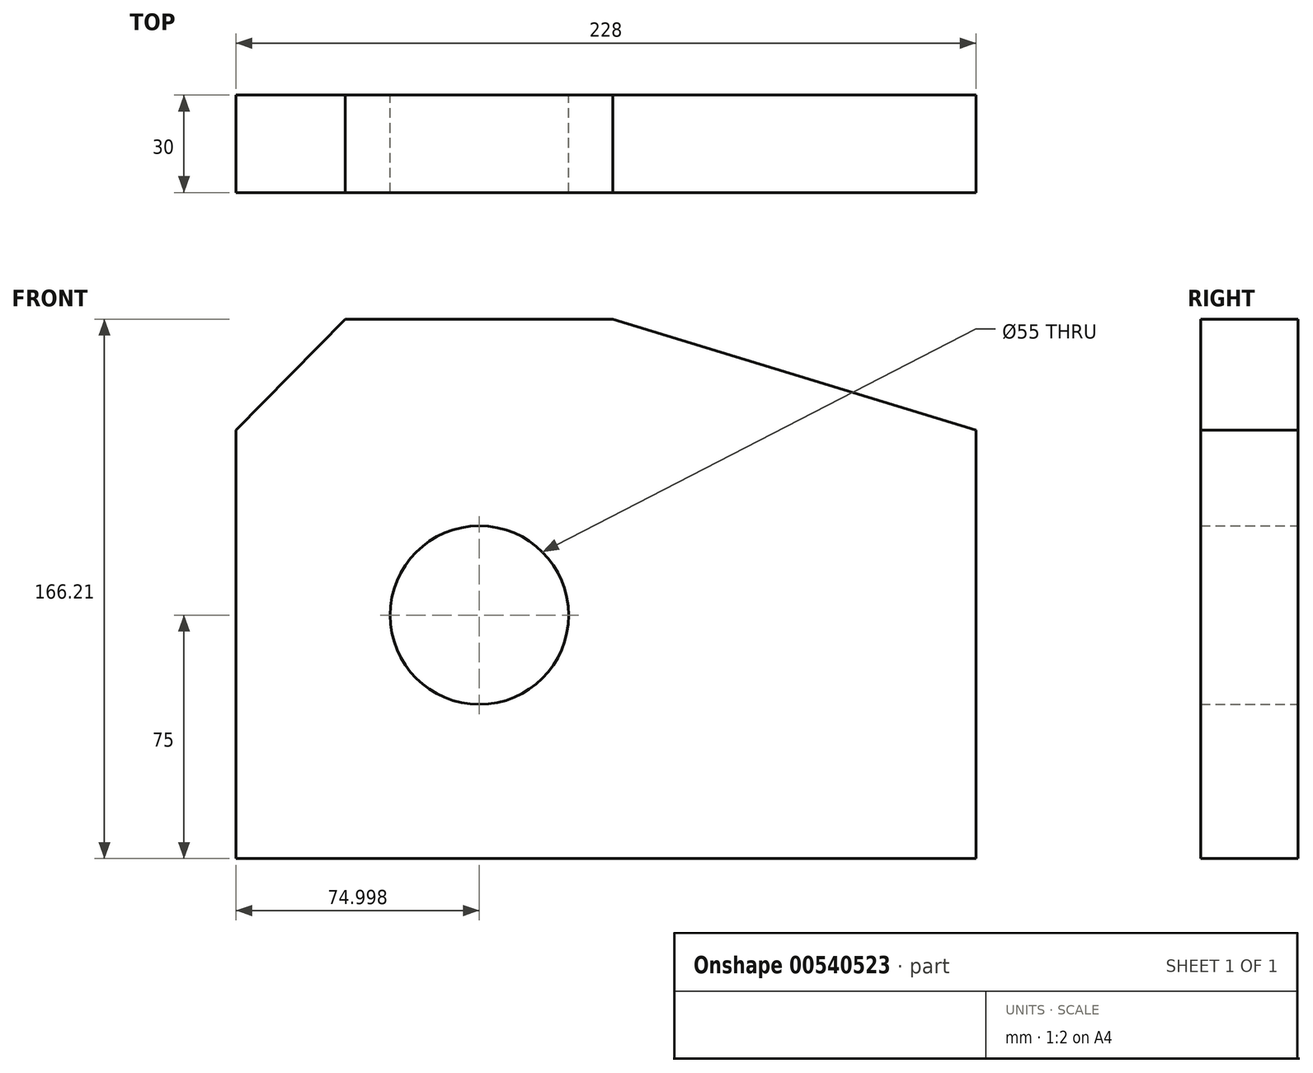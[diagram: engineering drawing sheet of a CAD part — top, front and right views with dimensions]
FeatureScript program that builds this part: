
annotation { "Feature Type Name" : "Feature", "Feature Type Description" : "" }
export const myFeature = defineFeature(function(context is Context, id is Id, definition is map)
    precondition{}
    {
        {
            var Q0;
            Q0=qCreatedBy(makeId("Front.planeOp"),FACE);
            var sketch = newSketch(context, id + "F0", { "sketchPlane" : qUnion([Q0])});
            skLineSegment(sketch, "E0", {"start": v(-113.2, -75) * mm, "end": v(114.8, -75) * mm});
            skLineSegment(sketch, "E1", {"start": v(114.8, -75) * mm, "end": v(114.8, 57) * mm});
            skLineSegment(sketch, "E2", {"start": v(114.8, 57) * mm, "end": v(2.92, 91.2) * mm});
            skLineSegment(sketch, "E3", {"start": v(2.92, 91.2) * mm, "end": v(-79.52, 91.2) * mm});
            skLineSegment(sketch, "E4", {"start": v(-79.52, 91.2) * mm, "end": v(-113.2, 57) * mm});
            skLineSegment(sketch, "E5", {"start": v(-113.2, 57) * mm, "end": v(-113.2, -75) * mm});
            skCircle(sketch, "E6", {"center": v(-38.2, 0) * mm, "radius": 27.5 * mm});
            skLineSegment(sketch, "E7", {"start": v(-38.2, -27.5) * mm, "end": v(-38.2, -36.83) * mm});
            skLineSegment(sketch, "E8", {"start": v(-113.2, -36.83) * mm, "end": v(-38.2, -36.83) * mm});
            skSolve(sketch);
        }
        {
            var Q0;
            {var subQ0=sQuery(id+"F0.wireOp",EDGE,"E0");Q0=makeQuery(id+"F0.imprint","IMPRINT",FACE,{"disambiguationData":[TD([[makeQuery(id+"F0.imprint","IMPRINT",EDGE,{"derivedFrom":subQ0}),1.0]])]});}
            extrude(context, id + "F1", {"entities" : qUnion([Q0]), "depth" : 30 * mm, "offsetDistance" : 25 * mm});
        }
    });
